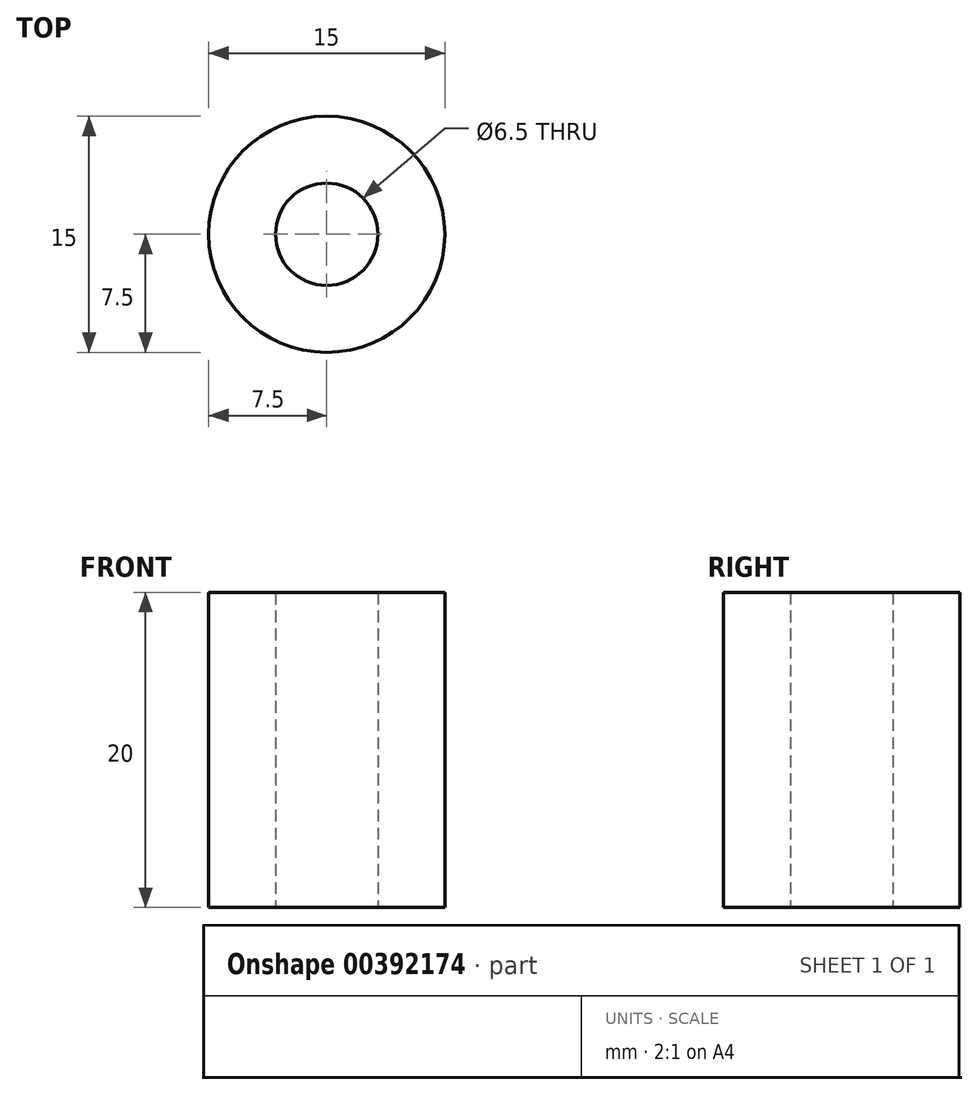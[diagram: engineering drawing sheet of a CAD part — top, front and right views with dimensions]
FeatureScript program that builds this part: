
annotation { "Feature Type Name" : "Feature", "Feature Type Description" : "" }
export const myFeature = defineFeature(function(context is Context, id is Id, definition is map)
    precondition{}
    {
        {
            var Q0;
            Q0=qCreatedBy(makeId("Top.planeOp"),FACE);
            var sketch = newSketch(context, id + "F0", { "sketchPlane" : qUnion([Q0])});
            skCircle(sketch, "E0", {"center": v(0, 0) * mm, "radius": 7.5 * mm});
            skCircle(sketch, "E1", {"center": v(0, 0) * mm, "radius": 3.25 * mm});
            skSolve(sketch);
        }
        {
            var Q0;
            Q0=makeQuery(id+"F0.imprint","IMPRINT",FACE,{"disambiguationData":[TD([[makeQuery(id+"F0.imprint","IMPRINT",EDGE,{"derivedFrom":sQuery(id+"F0.wireOp",EDGE,"E0")}),1.0]])]});
            extrude(context, id + "F1", {"entities" : qUnion([Q0]), "depth" : 20 * mm});
        }
    });
